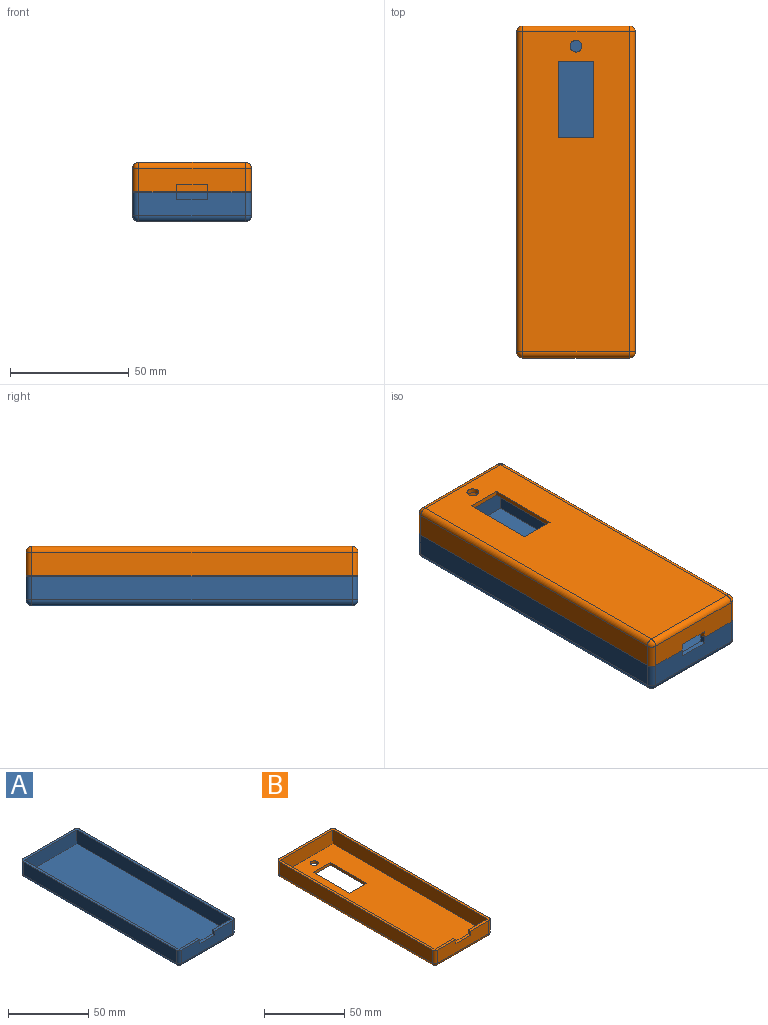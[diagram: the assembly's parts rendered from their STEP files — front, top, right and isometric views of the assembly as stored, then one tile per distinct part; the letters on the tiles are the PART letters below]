
ASSEMBLY  parts=2 mates=1
PART A: 26 faces, bbox 50x140x12.5 mm
  f0: plane 140x50mm, normal (0,0,1), area 712.6mm2, adj f1,f2,f3,f4,f5,f7,f8,f9
  f1: plane 45x10mm, normal (0,-1,0), area 411mm2, adj f0,f11,f12,f13,f19,f23,f25
  f2: plane 46x10.5mm, normal (0,1,0), area 444mm2, adj f0,f7,f9,f10,f11,f12,f13
  f3: plane 135x10mm, normal (1,0,0), area 1350mm2, adj f0,f16,f22,f25
  f4: plane 45x10mm, normal (0,1,0), area 450mm2, adj f0,f14,f16,f17
  f5: plane 135x10mm, normal (-1,0,0), area 1350mm2, adj f0,f14,f18,f19
  f6: plane 135x45mm, normal (0,0,-1), area 6075mm2, adj f17,f18,f22,f23
  f7: plane 136x10.5mm, normal (-1,0,0), area 1428mm2, adj f0,f2,f8,f10
  f8: plane 46x10.5mm, normal (0,-1,0), area 483mm2, adj f0,f7,f9,f10
  f9: plane 136x10.5mm, normal (1,0,0), area 1428mm2, adj f0,f2,f8,f10
  f10: plane 136x46mm, normal (0,0,1), area 6256mm2, adj f2,f7,f8,f9
  f11: plane 3x2mm, normal (-1,0,0), area 6mm2, adj f0,f1,f2,f13
  f12: plane 3x2mm, normal (1,0,0), area 6mm2, adj f0,f1,f2,f13
  f13: plane 13x2mm, normal (0,0,1), area 26mm2, adj f1,f2,f11,f12
  f14: cylinder r=2.5mm len=10mm, axis (0,0,1), area 39.3mm2, adj f0,f4,f5,f15
  f15: sphere r=2.5mm, area 9.8mm2, adj f14,f17,f18
  f16: cylinder r=2.5mm len=10mm, axis (0,0,-1), area 39.3mm2, adj f0,f3,f4,f20
  f17: cylinder r=2.5mm len=45mm, axis (-1,0,0), area 176.7mm2, adj f4,f6,f15,f20
  f18: cylinder r=2.5mm len=135mm, axis (0,-1,0), area 530.1mm2, adj f5,f6,f15,f21
  f19: cylinder r=2.5mm len=10mm, axis (0,0,-1), area 39.3mm2, adj f0,f1,f5,f21
  f20: sphere r=2.5mm, area 9.8mm2, adj f16,f17,f22
  f21: sphere r=2.5mm, area 9.8mm2, adj f18,f19,f23
  f22: cylinder r=2.5mm len=135mm, axis (0,1,0), area 530.1mm2, adj f3,f6,f20,f24
  f23: cylinder r=2.5mm len=45mm, axis (1,0,0), area 176.7mm2, adj f1,f6,f21,f24
  f24: sphere r=2.5mm, area 9.8mm2, adj f22,f23,f25
  f25: cylinder r=2.5mm len=10mm, axis (0,0,1), area 39.3mm2, adj f0,f1,f3,f24
PART B: 31 faces, bbox 50x140x12.5 mm
  f0: plane 135x45mm, normal (0,0,-1), area 5575.4mm2, adj f14,f15,f16,f17,f18,f22,f23,f27
  f1: plane 136x46mm, normal (0,0,1), area 5756.4mm2, adj f4,f8,f9,f10,f14,f15,f16,f17
  f2: plane 140x50mm, normal (0,0,1), area 712.6mm2, adj f3,f4,f5,f6,f7,f8,f9,f10
  f3: plane 45x10mm, normal (0,-1,0), area 411mm2, adj f2,f11,f12,f13,f24,f28,f30
  f4: plane 46x10.5mm, normal (0,1,0), area 444mm2, adj f1,f2,f8,f10,f11,f12,f13
  f5: plane 135x10mm, normal (1,0,0), area 1350mm2, adj f2,f21,f27,f30
  f6: plane 45x10mm, normal (0,1,0), area 450mm2, adj f2,f19,f21,f22
  f7: plane 135x10mm, normal (-1,0,0), area 1350mm2, adj f2,f19,f23,f24
  f8: plane 136x10.5mm, normal (-1,0,0), area 1428mm2, adj f1,f2,f4,f9
  f9: plane 46x10.5mm, normal (0,-1,0), area 483mm2, adj f1,f2,f8,f10
  f10: plane 136x10.5mm, normal (1,0,0), area 1428mm2, adj f1,f2,f4,f9
  f11: plane 3x2mm, normal (-1,0,0), area 6mm2, adj f2,f3,f4,f13
  f12: plane 3x2mm, normal (1,0,0), area 6mm2, adj f2,f3,f4,f13
  f13: plane 13x2mm, normal (0,0,1), area 26mm2, adj f3,f4,f11,f12
  f14: cylinder r=2.5mm len=5mm, axis (0,0,-1), area 31.4mm2, adj f0,f1
  f15: plane 15x2mm, normal (0,1,0), area 30mm2, adj f0,f1,f16,f18
  f16: plane 32x2mm, normal (1,0,0), area 64mm2, adj f0,f1,f15,f17
  f17: plane 15x2mm, normal (0,-1,0), area 30mm2, adj f0,f1,f16,f18
  f18: plane 32x2mm, normal (-1,0,0), area 64mm2, adj f0,f1,f15,f17
  f19: cylinder r=2.5mm len=10mm, axis (0,0,1), area 39.3mm2, adj f2,f6,f7,f20
  f20: sphere r=2.5mm, area 9.8mm2, adj f19,f22,f23
  f21: cylinder r=2.5mm len=10mm, axis (0,0,-1), area 39.3mm2, adj f2,f5,f6,f25
  f22: cylinder r=2.5mm len=45mm, axis (-1,0,0), area 176.7mm2, adj f0,f6,f20,f25
  f23: cylinder r=2.5mm len=135mm, axis (0,-1,0), area 530.1mm2, adj f0,f7,f20,f26
  f24: cylinder r=2.5mm len=10mm, axis (0,0,-1), area 39.3mm2, adj f2,f3,f7,f26
  f25: sphere r=2.5mm, area 9.8mm2, adj f21,f22,f27
  f26: sphere r=2.5mm, area 9.8mm2, adj f23,f24,f28
  f27: cylinder r=2.5mm len=135mm, axis (0,1,0), area 530.1mm2, adj f0,f5,f25,f29
  f28: cylinder r=2.5mm len=45mm, axis (1,0,0), area 176.7mm2, adj f0,f3,f26,f29
  f29: sphere r=2.5mm, area 9.8mm2, adj f27,f28,f30
  f30: cylinder r=2.5mm len=10mm, axis (0,0,1), area 39.3mm2, adj f2,f3,f5,f29
PLACE A t=(2.24,1.58,-5.79)mm
PLACE B rot(axis=(0,1,0),180deg) t=(2.24,1.58,19.21)mm
MATE fastened B.f2 <-> A.f0  axis (0,0,-1) through (2.24,4.1,6.71)mm
